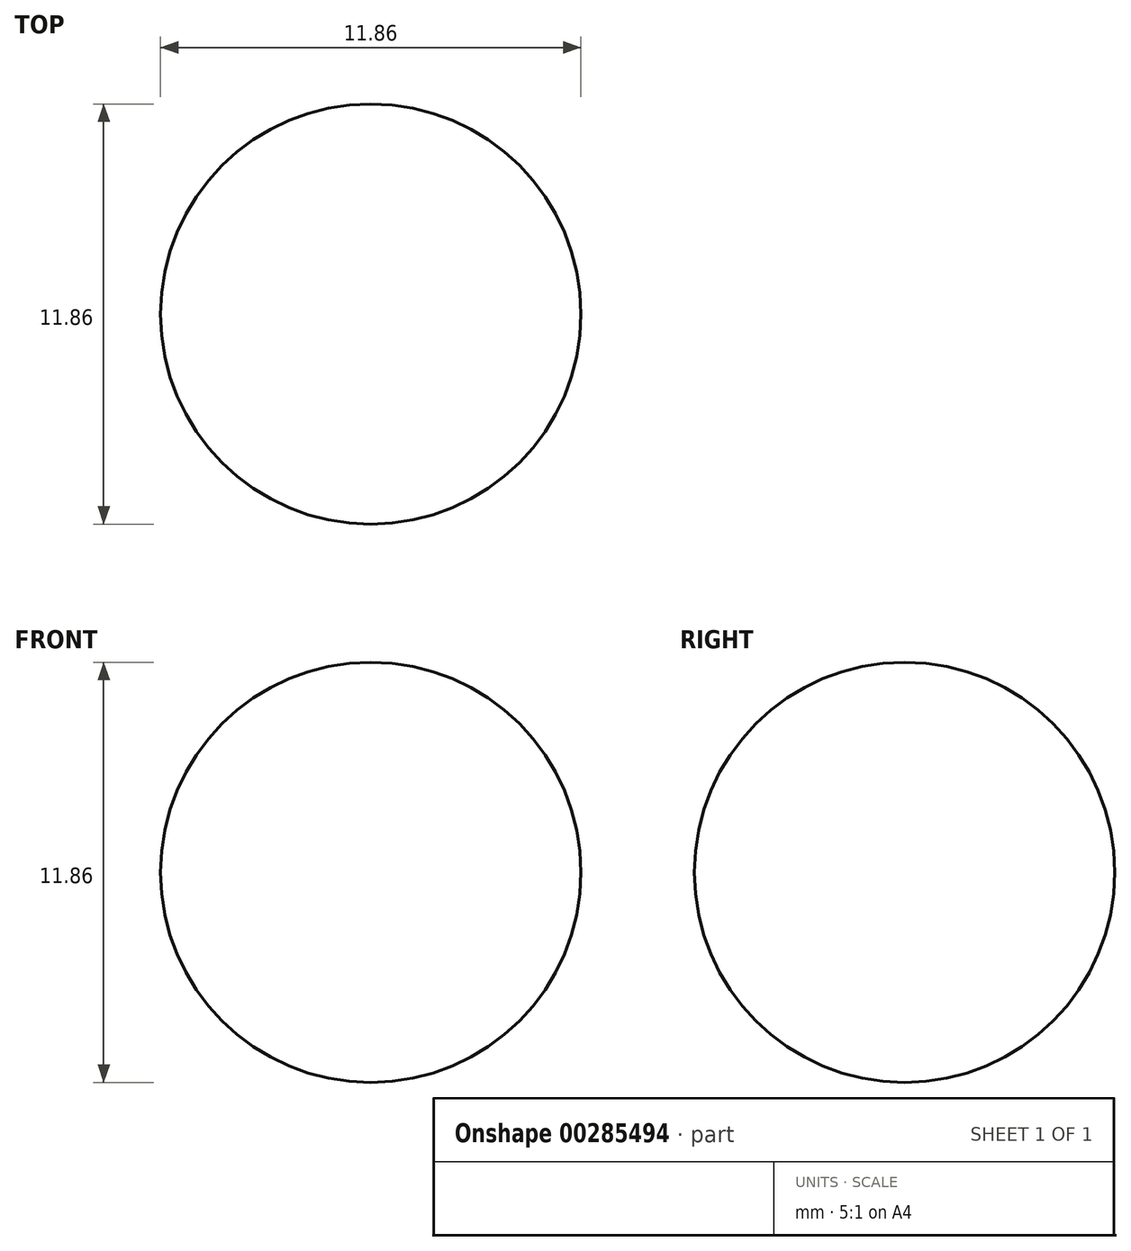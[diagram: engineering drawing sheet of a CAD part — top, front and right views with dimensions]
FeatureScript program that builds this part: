
annotation { "Feature Type Name" : "Feature", "Feature Type Description" : "" }
export const myFeature = defineFeature(function(context is Context, id is Id, definition is map)
    precondition{}
    {
        {
            var Q0;
            Q0=qCreatedBy(makeId("Top.planeOp"),FACE);
            var sketch = newSketch(context, id + "F0", { "sketchPlane" : qUnion([Q0])});
            skCircle(sketch, "E0", {"center": v(0, 0) * mm, "radius": 5.93 * mm});
            skLineSegment(sketch, "E1", {"start": v(0, 0) * mm, "end": v(5.93, 0) * mm});
            skLineSegment(sketch, "E2", {"start": v(5.93, 0) * mm, "end": v(-5.93, 0) * mm});
            skSolve(sketch);
        }
        {
            var Q0;
            {var subQ0=sQuery(id+"F0.wireOp",EDGE,"E2");var subQ4=makeQuery(id+"F0.imprint","IMPRINT",VERTEX,{"derivedFrom":subQ0});Q0=makeQuery(id+"F0.imprint","IMPRINT",FACE,{"disambiguationData":[TD([[makeQuery(id+"F0.imprint","IMPRINT",EDGE,{"disambiguationData":[TD([[subQ4,1.0]])],"derivedFrom":subQ0}),-1.0]])]});}
            var Q1;
            Q1=sQuery(id+"F0.wireOp",EDGE,"E2");
            revolve(context, id + "F1", {"entities" : qUnion([Q0]), "axis" : qUnion([Q1]), "revolveType" : RevolveType.FULL});
        }
    });
